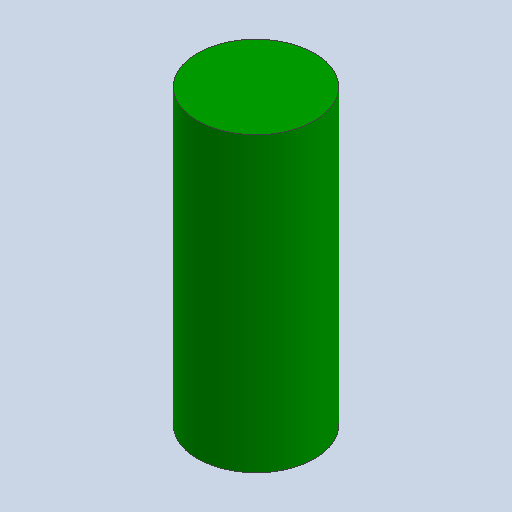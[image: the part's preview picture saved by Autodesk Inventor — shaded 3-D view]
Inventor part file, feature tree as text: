
AUTODESK INVENTOR PART (.ipt)
format: ipt  version: 2025.2 (Build 292293000, 293)  size: 89,600 bytes
history: native  units: in
note: dims shown in document units (in); Inventor stores cm internally (conversion verified against a paired STEP export)
features: other x3, sketch x1
ambient origin geometry x8: Origin, YZ Plane, XZ Plane, XY Plane, X Axis, Y Axis, Z Axis, Center Point
bodies: Solid1 (feature_tree)
feature tree (4):
  other  "26650(Green)_MIR3.ipt"
  other  "Solid1::26650(Green)_MIR3.ipt"
  other  "TaggingFeature1"
  sketch  "Sketch1"  dims[d0=0.3937in]
